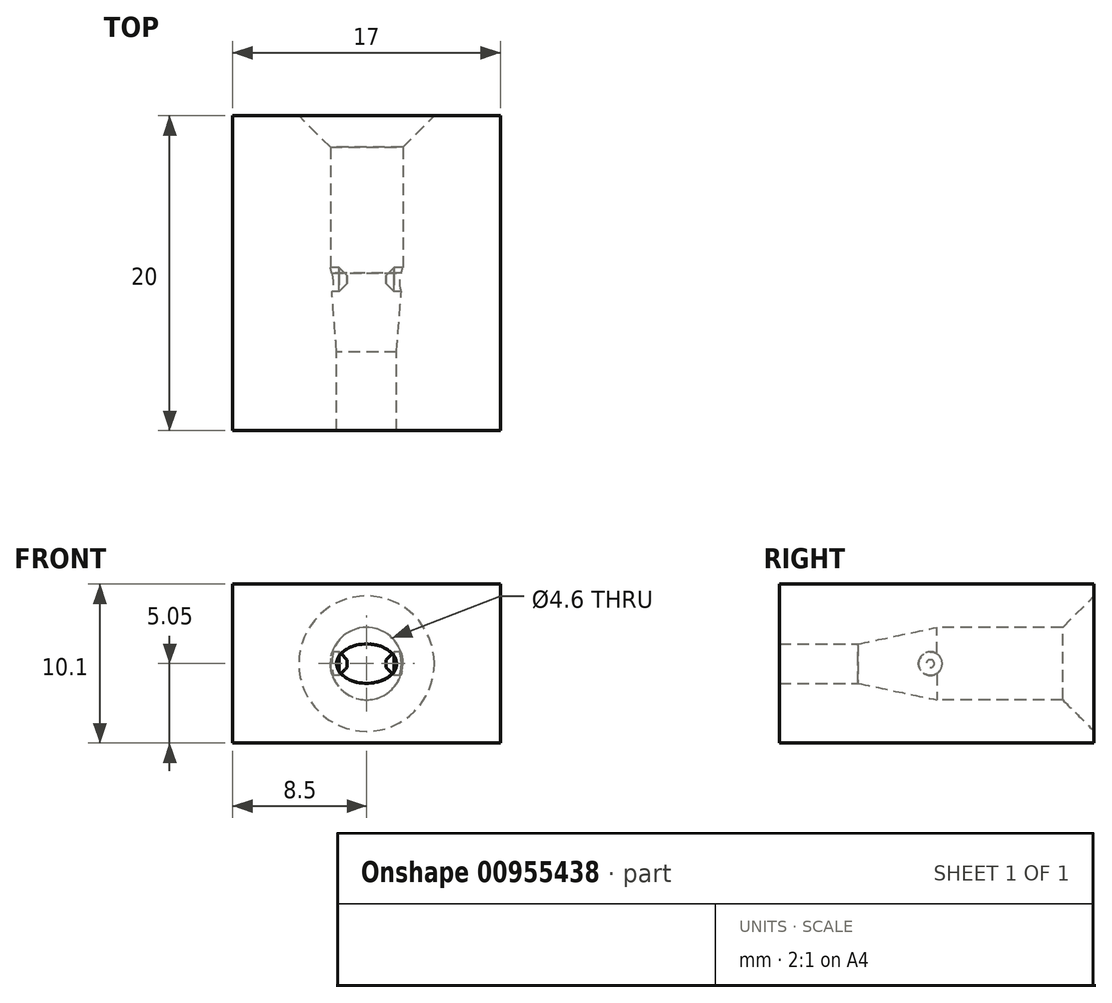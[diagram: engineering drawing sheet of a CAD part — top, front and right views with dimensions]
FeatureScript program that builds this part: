
annotation { "Feature Type Name" : "Feature", "Feature Type Description" : "" }
export const myFeature = defineFeature(function(context is Context, id is Id, definition is map)
    precondition{}
    {
        {
            var Q0;
            Q0=qCreatedBy(makeId("Front.planeOp"),FACE);
            var sketch = newSketch(context, id + "F0", { "sketchPlane" : qUnion([Q0])});
            skEllipse(sketch, "E0", {"center": v(0, 0) * mm, "majorRadius": 2.3 * mm, "minorRadius": 2.3 * mm, "majorAxis": v(1, 0)});
            skCircle(sketch, "E1", {"center": v(0, 0) * mm, "radius": 5 * mm});
            skSolve(sketch);
        }
        {
            var Q0;
            Q0=qCreatedBy(makeId("Front.planeOp"),FACE);
            cPlane(context, id + "F1", {"entities" : qUnion([Q0]), "cplaneType" : CPlaneType.OFFSET, "offset" : 5 * mm, "width" : 150 * mm, "height" : 150 * mm});
        }
        {
            var Q0;
            Q0=qCreatedBy(id+"F1.planeOp",FACE);
            var sketch = newSketch(context, id + "F2", { "sketchPlane" : qUnion([Q0])});
            skEllipse(sketch, "E2", {"center": v(0, 0) * mm, "majorRadius": 1.9 * mm, "minorRadius": 1.25 * mm, "majorAxis": v(1, 0)});
            skCircle(sketch, "E3", {"center": v(0, 0) * mm, "radius": 5 * mm});
            skSolve(sketch);
        }
        {
            var Q0;
            Q0=makeQuery(id+"F0.imprint","IMPRINT",FACE,{"disambiguationData":[TD([[makeQuery(id+"F0.imprint","IMPRINT",EDGE,{"derivedFrom":sQuery(id+"F0.wireOp",EDGE,"E0")}),-1.0]])]});
            var Q1;
            Q1=makeQuery(id+"F0.imprint","IMPRINT",FACE,{"disambiguationData":[TD([[makeQuery(id+"F0.imprint","IMPRINT",EDGE,{"derivedFrom":sQuery(id+"F0.wireOp",EDGE,"E0")}),1.0]])]});
            extrude(context, id + "F3", {"entities" : qUnion([Q0, Q1]), "depth" : 5 * mm, "offsetDistance" : 25 * mm});
        }
        {
            var Q1;
            Q1=makeQuery(id+"F2.imprint","IMPRINT",FACE,{"disambiguationData":[TD([[makeQuery(id+"F2.imprint","IMPRINT",EDGE,{"derivedFrom":sQuery(id+"F2.wireOp",EDGE,"E2")}),1.0]])]});
            var Q2;
            Q2=makeQuery(id+"F0.imprint","IMPRINT",FACE,{"disambiguationData":[TD([[makeQuery(id+"F0.imprint","IMPRINT",EDGE,{"derivedFrom":sQuery(id+"F0.wireOp",EDGE,"E0")}),1.0]])]});
            loft(context, id + "F4", {"operationType" : NewBodyOperationType.REMOVE, "sheetProfilesArray" : [{ "sheetProfileEntities" : qUnion([Q1]) }, { "sheetProfileEntities" : qUnion([Q2]) }]});
        }
        {
            var Q0;
            Q0=makeQuery(id+"F3.opExtrude","CAP_FACE",FACE,{"disambiguationData":[OSD([sQuery(id+"F0.wireOp",EDGE,"E1")])],"isStart":false});
            var sketch = newSketch(context, id + "F5", { "sketchPlane" : qUnion([Q0])});
            skCircle(sketch, "E4", {"center": v(0, 0) * mm, "radius": 5 * mm});
            skSolve(sketch);
        }
        {
            var Q0;
            Q0=makeQuery(id+"F5.imprint","IMPRINT",FACE,{"disambiguationData":[TD([[makeQuery(id+"F5.imprint","IMPRINT",EDGE,{"derivedFrom":sQuery(id+"F5.wireOp",EDGE,"E4")}),1.0]])]});
            var Q1;
            Q1=makeQuery(id+"F5.imprint","IMPRINT",FACE,{"disambiguationData":[TD([[makeQuery(id+"F5.imprint","IMPRINT",EDGE,{"derivedFrom":makeQuery(id+"F4.boolean.opBoolean","COPY",EDGE,{"derivedFrom":makeQuery(id+"F4.opLoft","MID_CAP_EDGE",EDGE,{"disambiguationData":[OSD([sQuery(id+"F2.wireOp",EDGE,"E2")])],"capPos":0.0})})}),-1.0]])]});
            extrude(context, id + "F6", {"entities" : qUnion([Q0, Q1]), "operationType" : NewBodyOperationType.ADD, "depth" : 5 * mm, "offsetDistance" : 25 * mm});
        }
        {
            var Q0;
            Q0=makeQuery(id+"F0.imprint","IMPRINT",FACE,{"disambiguationData":[TD([[makeQuery(id+"F0.imprint","IMPRINT",EDGE,{"derivedFrom":sQuery(id+"F0.wireOp",EDGE,"E0")}),-1.0]])]});
            extrude(context, id + "F7", {"entities" : qUnion([Q0]), "operationType" : NewBodyOperationType.ADD, "oppositeDirection" : true, "depth" : 10 * mm, "offsetDistance" : 25 * mm});
        }
        {
            var Q0;
            Q0=makeQuery(id+"F7.opExtrude","CAP_EDGE",EDGE,{"disambiguationData":[OSD([sQuery(id+"F0.wireOp",EDGE,"E0")])],"isStart":false});
            chamfer(context, id + "F8", {"entities" : qUnion([Q0]), "width" : 2 * mm, "tangentPropagation" : true});
        }
        {
            var Q0;
            Q0=qCreatedBy(makeId("Right.planeOp"),FACE);
            var sketch = newSketch(context, id + "F9", { "sketchPlane" : qUnion([Q0])});
            skCircle(sketch, "E5", {"center": v(-0.4, 0) * mm, "radius": 0.75 * mm});
            skSolve(sketch);
        }
        {
            var Q0;
            Q0=qSketchRegion(id+"F9",true);
            extrude(context, id + "F10", {"entities" : qUnion([Q0]), "operationType" : NewBodyOperationType.ADD, "depth" : 4.5 * mm, "offsetDistance" : 25 * mm, "hasSecondDirection" : true, "secondDirectionOppositeDirection" : true, "secondDirectionDepth" : 4.5 * mm});
        }
        {
            var Q0;
            Q0=qCreatedBy(makeId("Front.planeOp"),FACE);
            var sketch = newSketch(context, id + "F11", { "sketchPlane" : qUnion([Q0])});
            skLineSegment(sketch, "E6.bottom", {"start": v(-1.25, 0.75) * mm, "end": v(1.25, 0.75) * mm});
            skLineSegment(sketch, "E6.top", {"start": v(-1.25, -0.75) * mm, "end": v(1.25, -0.75) * mm});
            skLineSegment(sketch, "E6.left", {"start": v(-1.25, 0.75) * mm, "end": v(-1.25, -0.75) * mm});
            skLineSegment(sketch, "E6.right", {"start": v(1.25, 0.75) * mm, "end": v(1.25, -0.75) * mm});
            skPoint(sketch, "E6.middle", {"position": v(0, 0) * mm});
            skSolve(sketch);
        }
        {
            var Q0;
            Q0=makeQuery(id+"F11.imprint","IMPRINT",FACE,{"disambiguationData":[TD([[makeQuery(id+"F11.imprint","IMPRINT",EDGE,{"derivedFrom":sQuery(id+"F11.wireOp",EDGE,"E6.bottom")}),-1.0]])]});
            extrude(context, id + "F12", {"entities" : qUnion([Q0]), "operationType" : NewBodyOperationType.REMOVE, "depth" : 2 * mm, "offsetDistance" : 25 * mm, "hasSecondDirection" : true, "secondDirectionOppositeDirection" : true, "secondDirectionDepth" : 2 * mm});
        }
        {
            var Q0;
            Q0=makeQuery(id+"F12.boolean.opBoolean","INTERSECT",EDGE,{"derivedFrom":[makeQuery(id+"F10.opExtrude","SWEPT_FACE",FACE,{"disambiguationData":[OSD([sQuery(id+"F9.wireOp",EDGE,"E5")])]}),makeQuery(id+"F12.opExtrude","SWEPT_FACE",FACE,{"disambiguationData":[OSD([sQuery(id+"F11.wireOp",EDGE,"E6.right")])]})]});
            var Q1;
            Q1=makeQuery(id+"F12.boolean.opBoolean","INTERSECT",EDGE,{"derivedFrom":[makeQuery(id+"F10.opExtrude","SWEPT_FACE",FACE,{"disambiguationData":[OSD([sQuery(id+"F9.wireOp",EDGE,"E5")])]}),makeQuery(id+"F12.opExtrude","SWEPT_FACE",FACE,{"disambiguationData":[OSD([sQuery(id+"F11.wireOp",EDGE,"E6.left")])]})]});
            chamfer(context, id + "F13", {"entities" : qUnion([Q0, Q1]), "width" : 0.5 * mm, "tangentPropagation" : true});
        }
        {
            var Q0;
            Q0=makeQuery(id+"F6.opExtrude","CAP_FACE",FACE,{"disambiguationData":[OSD([sQuery(id+"F5.wireOp",EDGE,"E4")])],"isStart":false});
            var sketch = newSketch(context, id + "F14", { "sketchPlane" : qUnion([Q0])});
            skLineSegment(sketch, "E7.bottom", {"start": v(8.5, 5.05) * mm, "end": v(-8.5, 5.05) * mm});
            skLineSegment(sketch, "E7.top", {"start": v(8.5, -5.05) * mm, "end": v(-8.5, -5.05) * mm});
            skLineSegment(sketch, "E7.left", {"start": v(8.5, 5.05) * mm, "end": v(8.5, -5.05) * mm});
            skLineSegment(sketch, "E7.right", {"start": v(-8.5, 5.05) * mm, "end": v(-8.5, -5.05) * mm});
            skPoint(sketch, "E7.middle", {"position": v(0, 0) * mm});
            skSolve(sketch);
        }
        {
            var Q0;
            {var subQ0=sQuery(id+"F14.wireOp",EDGE,"E7.left");Q0=makeQuery(id+"F14.imprint","IMPRINT",FACE,{"disambiguationData":[TD([[makeQuery(id+"F14.imprint","IMPRINT",EDGE,{"derivedFrom":subQ0}),-1.0]])]});}
            var Q1;
            {var subQ0=sQuery(id+"F14.wireOp",EDGE,"E7.right");Q1=makeQuery(id+"F14.imprint","IMPRINT",FACE,{"disambiguationData":[TD([[makeQuery(id+"F14.imprint","IMPRINT",EDGE,{"derivedFrom":subQ0}),1.0]])]});}
            extrude(context, id + "F15", {"entities" : qUnion([Q0, Q1]), "operationType" : NewBodyOperationType.ADD, "oppositeDirection" : true, "depth" : 20 * mm, "offsetDistance" : 25 * mm});
        }
    });
